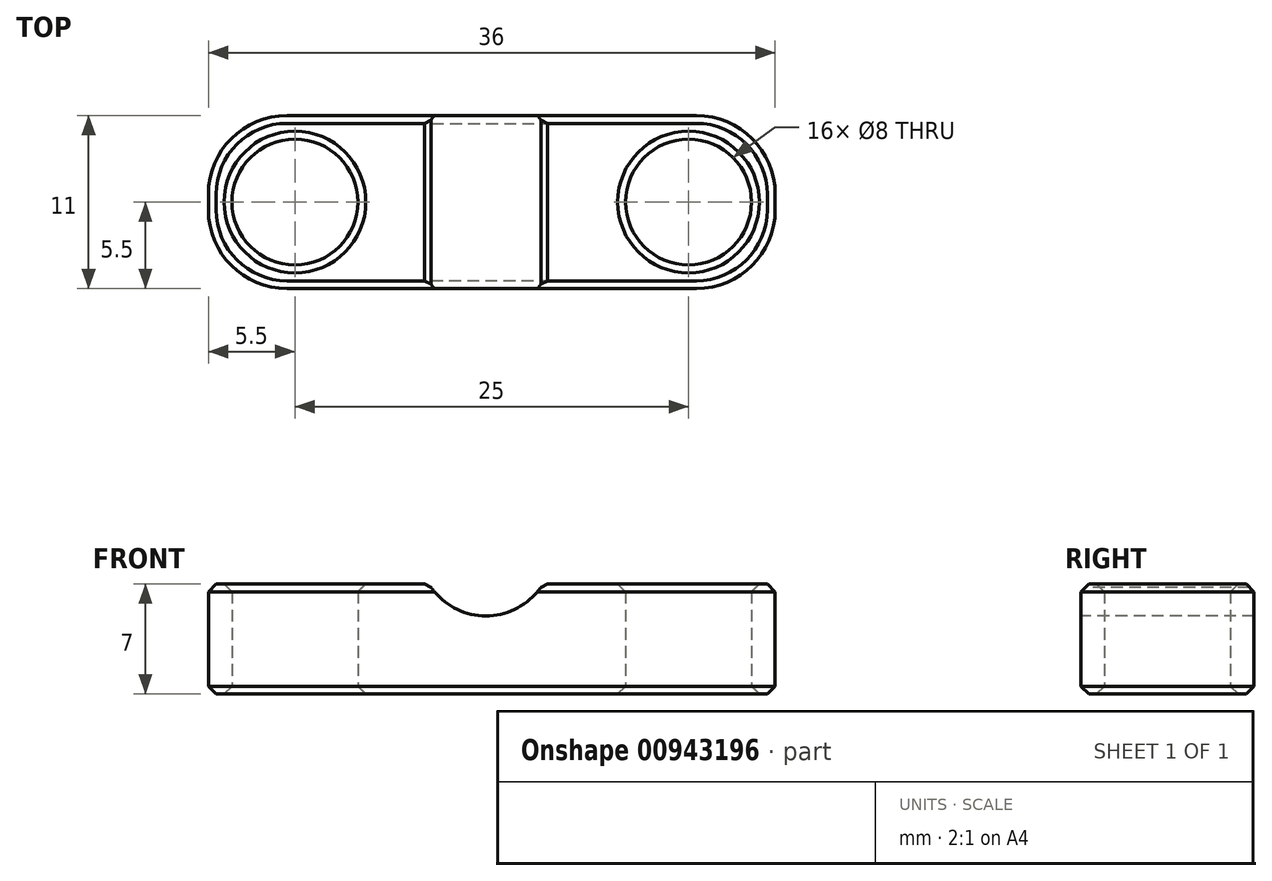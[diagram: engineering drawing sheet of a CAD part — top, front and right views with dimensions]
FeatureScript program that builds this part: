
annotation { "Feature Type Name" : "Feature", "Feature Type Description" : "" }
export const myFeature = defineFeature(function(context is Context, id is Id, definition is map)
    precondition{}
    {
        {
            var Q0;
            Q0=qCreatedBy(makeId("Top.planeOp"),FACE);
            var sketch = newSketch(context, id + "F0", { "sketchPlane" : qUnion([Q0])});
            skLineSegment(sketch, "E0.bottom", {"start": v(-0.5, 5.5) * mm, "end": v(25.5, 5.5) * mm});
            skLineSegment(sketch, "E0.top", {"start": v(-0.5, -5.5) * mm, "end": v(25.5, -5.5) * mm});
            skLineSegment(sketch, "E0.left", {"start": v(-5.5, 0.5) * mm, "end": v(-5.5, -0.5) * mm});
            skLineSegment(sketch, "E0.right", {"start": v(30.5, 0.5) * mm, "end": v(30.5, -0.5) * mm});
            skCircle(sketch, "E1", {"center": v(0, 0) * mm, "radius": 4 * mm});
            skCircle(sketch, "E2", {"center": v(25, 0) * mm, "radius": 4 * mm});
            skPoint(sketch, "E3.visualSharp", {"position": v(-5.5, 5.5) * mm});
            skArc(sketch, "E3.filletArc", {"start": v(-0.5, 5.5) * mm, "mid": v(-4.04, 4.04) * mm, "end": v(-5.5, 0.5) * mm});
            skPoint(sketch, "E4.visualSharp", {"position": v(30.5, 5.5) * mm});
            skArc(sketch, "E4.filletArc", {"start": v(30.5, 0.5) * mm, "mid": v(29.04, 4.04) * mm, "end": v(25.5, 5.5) * mm});
            skPoint(sketch, "E5.visualSharp", {"position": v(30.5, -5.5) * mm});
            skArc(sketch, "E5.filletArc", {"start": v(25.5, -5.5) * mm, "mid": v(29.04, -4.04) * mm, "end": v(30.5, -0.5) * mm});
            skPoint(sketch, "E6.visualSharp", {"position": v(-5.5, -5.5) * mm});
            skArc(sketch, "E6.filletArc", {"start": v(-5.5, -0.5) * mm, "mid": v(-4.04, -4.04) * mm, "end": v(-0.5, -5.5) * mm});
            skSolve(sketch);
        }
        {
            var Q0;
            Q0=qSketchRegion(id+"F0",true);
            extrude(context, id + "F1", {"entities" : qUnion([Q0]), "depth" : 7 * mm, "offsetDistance" : 25 * mm});
        }
        {
            var Q0;
            Q0=makeQuery(id+"F1.opExtrude","SWEPT_FACE",FACE,{"disambiguationData":[OSD([sQuery(id+"F0.wireOp",EDGE,"E0.top")])]});
            var sketch = newSketch(context, id + "F2", { "sketchPlane" : qUnion([Q0])});
            skArc(sketch, "E7", {"start": v(8.5, 7) * mm, "mid": v(12.13, 4.96) * mm, "end": v(15.76, 7) * mm});
            skSolve(sketch);
        }
        {
            var Q0;
            Q0=qSketchRegion(id+"F2",true);
            var Q1;
            {var subQ0=sQuery(id+"F2.wireOp",EDGE,"E7");Q1=makeQuery(id+"F2.imprint","IMPRINT",FACE,{"disambiguationData":[TD([[makeQuery(id+"F2.imprint","IMPRINT",EDGE,{"derivedFrom":subQ0}),1.0]])]});}
            extrude(context, id + "F3", {"entities" : qUnion([Q0, Q1]), "operationType" : NewBodyOperationType.REMOVE, "oppositeDirection" : true, "depth" : 25 * mm, "offsetDistance" : 25 * mm});
        }
        {
            var Q0;
            Q0=makeQuery(id+"F1.opExtrude","CAP_EDGE",EDGE,{"disambiguationData":[OSD([sQuery(id+"F0.wireOp",EDGE,"E0.top")])],"isStart":true});
            var Q1;
            Q1=makeQuery(id+"F1.opExtrude","CAP_FACE",FACE,{"disambiguationData":[OSD([sQuery(id+"F0.wireOp",EDGE,"E0.bottom"),sQuery(id+"F0.wireOp",EDGE,"E0.top"),sQuery(id+"F0.wireOp",EDGE,"E0.left"),sQuery(id+"F0.wireOp",EDGE,"E0.right"),sQuery(id+"F0.wireOp",EDGE,"E1"),sQuery(id+"F0.wireOp",EDGE,"E2"),sQuery(id+"F0.wireOp",EDGE,"E3.filletArc"),sQuery(id+"F0.wireOp",EDGE,"E4.filletArc"),sQuery(id+"F0.wireOp",EDGE,"E5.filletArc"),sQuery(id+"F0.wireOp",EDGE,"E6.filletArc")])],"isStart":true});
            var Q2;
            {var subQ0=sQuery(id+"F0.wireOp",EDGE,"E1");var subQ1=sQuery(id+"F0.wireOp",EDGE,"E0.left");var subQ2=sQuery(id+"F0.wireOp",EDGE,"E0.top");var subQ3=sQuery(id+"F0.wireOp",EDGE,"E0.bottom");var subQ4=sQuery(id+"F0.wireOp",EDGE,"E6.filletArc");var subQ5=sQuery(id+"F0.wireOp",EDGE,"E3.filletArc");Q2=makeQuery(id+"F3.boolean.opBoolean","SPLIT",FACE,{"disambiguationData":[TD([makeQuery(id+"F1.opExtrude","SWEPT_FACE",FACE,{"disambiguationData":[OSD([subQ1])]})])],"derivedFrom":makeQuery(id+"F1.opExtrude","CAP_FACE",FACE,{"disambiguationData":[OSD([subQ3,subQ2,subQ1,sQuery(id+"F0.wireOp",EDGE,"E0.right"),subQ0,sQuery(id+"F0.wireOp",EDGE,"E2"),subQ5,sQuery(id+"F0.wireOp",EDGE,"E4.filletArc"),sQuery(id+"F0.wireOp",EDGE,"E5.filletArc"),subQ4])],"isStart":false})});}
            var Q3;
            {var subQ0=sQuery(id+"F0.wireOp",EDGE,"E2");var subQ1=sQuery(id+"F0.wireOp",EDGE,"E0.top");var subQ2=sQuery(id+"F0.wireOp",EDGE,"E0.right");var subQ3=sQuery(id+"F0.wireOp",EDGE,"E0.bottom");var subQ4=sQuery(id+"F0.wireOp",EDGE,"E4.filletArc");var subQ5=sQuery(id+"F0.wireOp",EDGE,"E5.filletArc");Q3=makeQuery(id+"F3.boolean.opBoolean","SPLIT",FACE,{"disambiguationData":[TD([makeQuery(id+"F1.opExtrude","SWEPT_FACE",FACE,{"disambiguationData":[OSD([subQ2])]})])],"derivedFrom":makeQuery(id+"F1.opExtrude","CAP_FACE",FACE,{"disambiguationData":[OSD([subQ3,subQ1,sQuery(id+"F0.wireOp",EDGE,"E0.left"),subQ2,sQuery(id+"F0.wireOp",EDGE,"E1"),subQ0,sQuery(id+"F0.wireOp",EDGE,"E3.filletArc"),subQ4,subQ5,sQuery(id+"F0.wireOp",EDGE,"E6.filletArc")])],"isStart":false})});}
            chamfer(context, id + "F4", {"entities" : qUnion([Q0, Q1, Q2, Q3]), "width" : 0.5 * mm, "tangentPropagation" : true});
        }
    });
